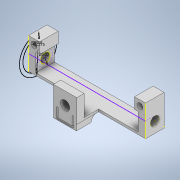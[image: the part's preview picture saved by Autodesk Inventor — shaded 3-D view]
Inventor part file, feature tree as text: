
AUTODESK INVENTOR PART (.ipt)
format: ipt  version: 2020 (Build 240168000, 168)  size: 284,672 bytes
history: native  units: mm
features: sketch x25, extrude x15, fillet x1
ambient origin geometry x8: Origin, YZ Plane, XZ Plane, XY Plane, X Axis, Y Axis, Z Axis, Center Point
bodies: Solid1 (feature_tree)
feature tree (41):
  sketch  "Sketch1"  dims[d3=25.4mm d4=25.4mm]
  extrude  "Extrusion1"  Depth=25.4mm
  extrude  "Extrusion2"  Depth=10.0mm TaperAngle=0.0deg
  extrude  "Extrusion3"  Depth=15.0mm
  sketch  "Sketch5"  dims[d14=14.85mm d15=0.0mm d16=20.32mm]
  sketch  "Sketch6"  dims[d17=41.275mm d18=2.0mm]
  extrude  "Extrusion4"  Depth=25.4mm TaperAngle=0.0deg
  sketch  "Sketch8"  dims[d24=10.0mm d25=0.0mm d26=15.0mm]
  extrude  "Extrusion5"  Depth=20.32mm
  extrude  "Extrusion6"  Depth=2.0mm
  sketch  "Sketch11"  dims[d32=25.4mm d33=0.0mm d34=7.4mm]
  extrude  "Extrusion7"  Depth=150.0mm TaperAngle=0.0deg
  extrude  "Extrusion8"  Depth=15.0mm
  extrude  "Extrusion9"  Depth=8.0mm
  sketch  "Sketch14"  dims[d42=25.0mm d43=10.0mm d44=0.0mm]
  sketch  "Sketch15"  dims[d45=31.75mm d46=10.0mm d47=0.0mm d48=12.7mm]
  sketch  "Sketch16"  dims[d49=10.0mm d50=0.0mm]
  extrude  "Extrusion10"  Depth=18.0mm
  extrude  "Extrusion11"  Depth=7.4mm
  sketch  "Sketch19"  dims[d59=1.5875mm]
  sketch  "Sketch20"  dims[d60=1.5875mm]
  extrude  "Extrusion12"  Depth=14.9mm TaperAngle=0.0deg
  extrude  "Extrusion13"  Depth=20.0mm TaperAngle=0.0deg
  sketch  "Sketch23"  dims[d63=8.0mm]
  sketch  "Sketch24"  dims[d64=20.0mm d65=0.0mm]
  extrude  "Extrusion14"  Depth=10.0mm TaperAngle=0.0deg
  extrude  "Extrusion15"  Depth=10.0mm TaperAngle=0.0deg
  fillet  "Fillet1"  Radius=12.7mm
  sketch  "Sketch2"  dims[d5=12.7mm d6=10.0mm d7=0.0mm]
  sketch  "Sketch3"  dims[d8=15.0mm d9=15.0mm]
  sketch  "Sketch4"  dims[d10=8.0mm d11=25.4mm d12=0.0mm]
  sketch  "Sketch7"  dims[d19=3.25mm d20=150.0mm d21=10.0mm d22=0.0mm d23=0.0mm]
  sketch  "Sketch9"  dims[d27=15.0mm d28=8.0mm]
  sketch  "Sketch10"  dims[d29=25.4mm d30=0.0mm d31=18.0mm]
  sketch  "Sketch12"  dims[d35=14.9mm d36=0.0mm d37=14.9mm d38=0.0mm]
  sketch  "Sketch13"  dims[d39=31.75mm d40=20.0mm d41=0.0mm]
  sketch  "Sketch17"  dims[d51=21.0mm]
  sketch  "Sketch18"  dims[d58=1.5875mm]
  sketch  "Sketch21"  dims[d61=6.35mm]
  sketch  "Sketch22"  dims[d62=50.8mm]
  sketch  "Sketch25"  dims[d66=15.0mm d67=0.0mm d68=9.0mm]
